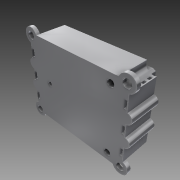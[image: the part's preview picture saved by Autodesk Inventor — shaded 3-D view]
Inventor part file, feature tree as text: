
AUTODESK INVENTOR PART (.ipt)
format: ipt  version: 2014 (Build 180170000, 170)  size: 982,016 bytes
history: native  units: mm
features: extrude x17, sketch x10, fillet x5, mirror x5, projected_geometry x3, plane x1, pattern_circular x1, revolve x1, chamfer x1
ambient origin geometry x8: Origin, YZ Plane, XZ Plane, XY Plane, X Axis, Y Axis, Z Axis, Center Point
bodies: Solid1 (feature_tree)
feature tree (44):
  extrude  "Base"  Depth=6.0mm
  extrude  "Floor & Servo Walls"  Depth=3.0mm
  plane  "Work Plane2"
  extrude  "Framing"  Depth=3.0mm
  fillet  "Fillet2"  Radius=150.0mm
  extrude  "Potentiometer Housing"  Depth=71.0mm
  extrude  "Centre Nail Mount"  Depth=30.0mm
  extrude  "Extrusion7"  Depth=35.0mm TaperAngle=0.0deg
  pattern_circular  "Circular Pattern1"  [2 undecoded]
  revolve  "Revolution1"  [1 undecoded]
  fillet  "Fillet5"  Radius=12.0mm
  fillet  "Fillet6"  Radius=12.0mm
  fillet  "Fillet7"  Radius=12.0mm
  fillet  "Fillet4"  Radius=24.0mm
  extrude  "Extrusion8"  Depth=3.0mm
  sketch  "Sketch8"  dims[d22=10.0mm d23=10.0mm d25=71.0mm]
  extrude  "Extrusion9"  Depth=3.0mm
  extrude  "Extrusion10"  Depth=3.0mm
  mirror  "Mirror1"
  mirror  "Mirror2"
  chamfer  "Chamfer1"  Distance=10.0mm
  sketch  "Sketch10"  dims[d26=30.0mm d27=54.5mm d28=54.5mm]
  extrude  "Extrusion12"  Depth=24.0mm
  extrude  "Extrusion13"  Depth=4.0mm
  extrude  "Extrusion14"  Depth=90.0mm
  mirror  "Mirror3"
  extrude  "Extrusion15"  Depth=90.0mm
  extrude  "Extrusion16"  Depth=2.0mm
  extrude  "Extrusion17"  Depth=2.0mm
  mirror  "Mirror4"
  extrude  "Extrusion18"  Depth=2.0mm
  extrude  "Extrusion19"  Depth=2.0mm
  mirror  "Mirror5"
  sketch  "Sketch3"  dims[d1=6.0mm d2=6.0mm d3=6.0mm]
  sketch  "Sketch5"  dims[d4=6.0mm d5=3.0mm]
  sketch  "Sketch7"  dims[d6=3.0mm d7=3.0mm d16=150.0mm d17=70.0mm]
  projected_geometry  "Projected Loop2"
  sketch  "Sketch11"  dims[d29=5.0mm d30=0.0mm d31=35.0mm d32=0.0mm]
  sketch  "Sketch12"  dims[d35=14.0mm]
  sketch  "Sketch13"  dims[d36=3.0mm]
  sketch  "Sketch14"  dims[d37=3.0mm]
  projected_geometry  "Projected Loop3"
  projected_geometry  "Projected Loop4"
  sketch  "Sketch15"  dims[d38=3.0mm d39=3.0mm d45=12.0mm d46=12.0mm d47=12.0mm d48=12.0mm d49=24.0mm d51=3.0mm d52=3.0mm d53=3.0mm d54=10.0mm d55=0.0mm d67=24.0mm d69=4.0mm d75=9.55mm d76=9.55mm d79=2.0mm d80=2.0mm d81=2.0mm d82=2.0mm d83=12.0mm d84=0.0mm d85=11.0mm d86=2.0mm d87=3.0mm d88=3.0mm d89=3.0mm d90=3.0mm d91=2.0mm d92=0.0mm d97=40.0mm d98=0.0mm d99=40.0mm d100=360.0deg d103=1.5mm d104=6.0mm d105=35.0mm d106=10.0mm d107=90.0deg d108=2.0mm d109=2.0mm d111=4.0mm d112=10.0mm d113=1.0mm d114=2.0mm d115=10.0mm d116=20.0mm d118=10.0mm d119=20.0mm d120=10.0mm d121=20.0mm d122=10.0mm d123=20.374355mm d125=30.0mm d126=30.0mm d127=30.0mm d128=30.0mm d131=6.0mm d132=6.0mm d133=6.0mm d134=6.0mm d135=10.0mm d136=10.0mm d137=3.0mm d139=3.0mm d140=3.0mm d141=3.0mm d142=3.0mm d143=3.0mm d144=3.0mm d145=3.0mm d146=140.0mm d147=3.0mm d148=6.35mm d149=4.0mm d150=8.726646mm d151=8.726646mm d152=2.0mm d153=2.0mm d154=2.0mm d155=2.0mm d156=1.0mm d157=2.0mm d158=2.0mm d159=35.0mm d160=4.775mm d161=4.775mm d171=5.0mm d172=0.0mm d173=3.38105mm d174=3.38105mm d175=6.0mm d176=4.1656mm d177=5.0mm d178=15.0mm d181=40.0mm d182=0.0mm d183=20.0mm d184=0.0mm d187=1.0mm d188=5.0mm d189=2.0mm d190=45.0deg d191=8.2804mm d192=6.1989mm d193=6.1989mm d196=5.207mm d197=5.207mm d200=12.3952mm d201=1.328045mm d202=1.328045mm d203=1.328045mm d204=1.328045mm d205=4.1402mm d206=4.1402mm d207=7.4434mm d208=0.0mm d210=15.0mm d211=0.0mm d212=40.0mm d213=0.0mm d214=80.0mm d215=0.0mm d216=8.509mm d221=5.334mm d222=3.0mm d223=0.0mm d224=15.0mm d226=15.0mm d227=18.0mm d228=5.0mm d229=8.509mm d230=5.0mm d231=0.0mm d232=6.35mm d233=1.6mm d234=1.6mm d235=1.6mm d236=1.6mm d237=5.0mm d238=0.0mm d239=5.0mm d240=5.0mm d241=5.0mm d242=5.0mm d243=4.0mm d244=4.0mm d245=4.0mm d246=4.0mm d247=4.0mm d248=1.5mm d249=1.5mm d250=3.0mm d251=90.0mm d252=0.0mm d253=10.0mm d254=3.0mm d255=1.5mm d256=1.5mm d257=2.0mm d258=10.0mm d259=10.0mm d260=2.0mm d261=5.0mm d262=90.0mm d263=0.0mm]
note: 3 required parameter values undecoded (feature->parameter linkage not recoverable at this tier; creation-order binding heuristic only, values carry confidence <= 0.55)